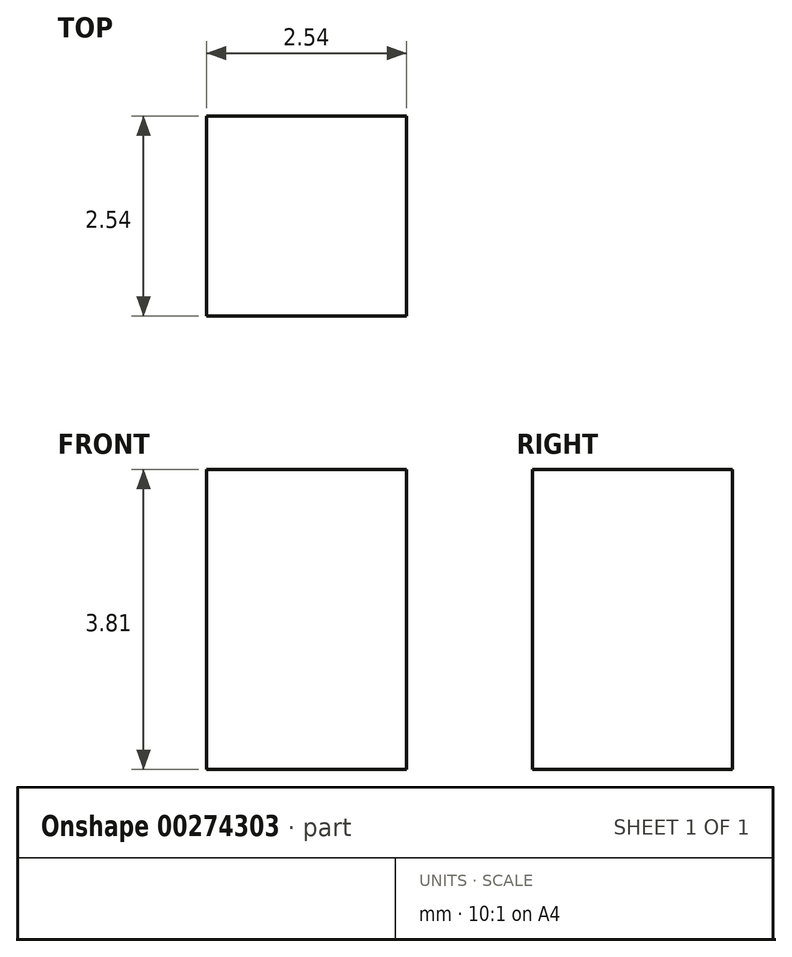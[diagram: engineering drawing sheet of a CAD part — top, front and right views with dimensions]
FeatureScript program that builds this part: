
annotation { "Feature Type Name" : "Feature", "Feature Type Description" : "" }
export const myFeature = defineFeature(function(context is Context, id is Id, definition is map)
    precondition{}
    {
        {
            var Q0;
            Q0=qCreatedBy(makeId("Top.planeOp"),FACE);
            var sketch = newSketch(context, id + "F0", { "sketchPlane" : qUnion([Q0])});
            skLineSegment(sketch, "E0.bottom", {"start": v(-1.27, -1.27) * mm, "end": v(1.27, -1.27) * mm});
            skLineSegment(sketch, "E0.top", {"start": v(-1.27, 1.27) * mm, "end": v(1.27, 1.27) * mm});
            skLineSegment(sketch, "E0.left", {"start": v(-1.27, -1.27) * mm, "end": v(-1.27, 1.27) * mm});
            skLineSegment(sketch, "E0.right", {"start": v(1.27, -1.27) * mm, "end": v(1.27, 1.27) * mm});
            skPoint(sketch, "E0.middle", {"position": v(0, 0) * mm});
            skSolve(sketch);
        }
        {
            var Q0;
            Q0=makeQuery(id+"F0.imprint","IMPRINT",FACE,{"disambiguationData":[TD([[makeQuery(id+"F0.imprint","IMPRINT",EDGE,{"derivedFrom":sQuery(id+"F0.wireOp",EDGE,"E0.bottom")}),1.0]])]});
            extrude(context, id + "F1", {"entities" : qUnion([Q0]), "oppositeDirection" : true, "depth" : 3.8 * mm});
        }
    });
